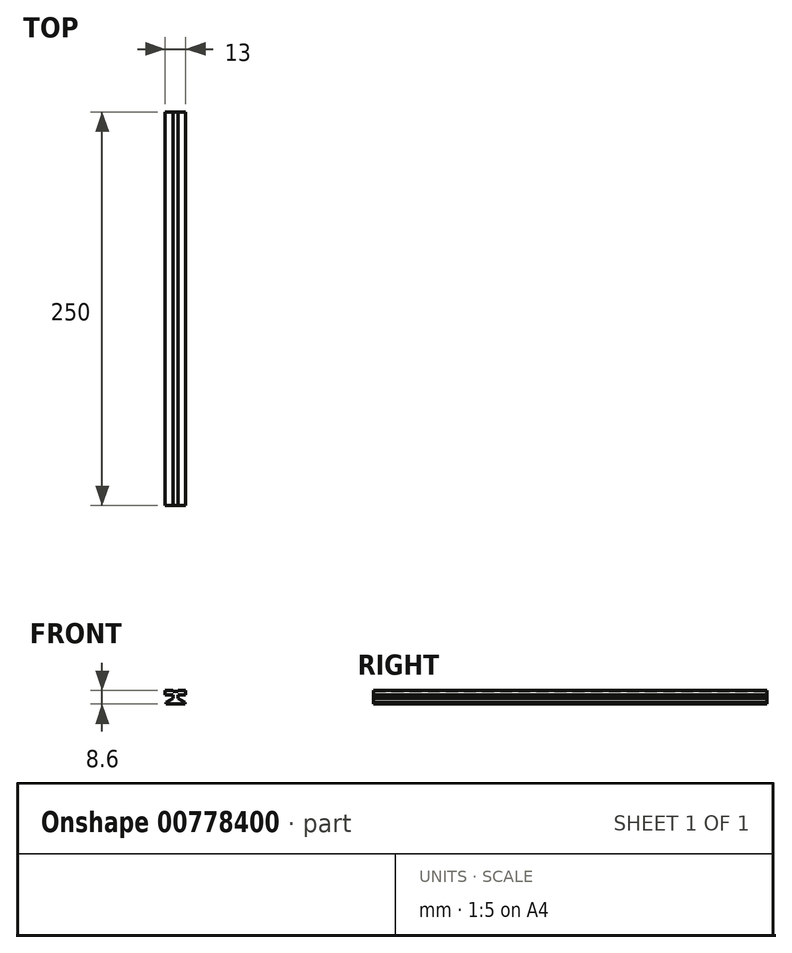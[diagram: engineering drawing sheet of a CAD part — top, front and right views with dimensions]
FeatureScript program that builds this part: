
annotation { "Feature Type Name" : "Feature", "Feature Type Description" : "" }
export const myFeature = defineFeature(function(context is Context, id is Id, definition is map)
    precondition{}
    {
        {
            var Q0;
            Q0=qCreatedBy(makeId("Front.planeOp"),FACE);
            var sketch = newSketch(context, id + "F0", { "sketchPlane" : qUnion([Q0])});
            skLineSegment(sketch, "E0.bottom", {"start": v(6, 0) * mm, "end": v(-6, 0) * mm});
            skLineSegment(sketch, "E0.top", {"start": v(6, 1) * mm, "end": v(-6, 1) * mm});
            skLineSegment(sketch, "E0.left", {"start": v(6, 0) * mm, "end": v(6, 1) * mm});
            skLineSegment(sketch, "E0.right", {"start": v(-6, 0) * mm, "end": v(-6, 1) * mm});
            skLineSegment(sketch, "E1", {"start": v(0, 0) * mm, "end": v(0, 5.9) * mm});
            skLineSegment(sketch, "E2", {"start": v(0, 5.9) * mm, "end": v(0, 8.6) * mm});
            skLineSegment(sketch, "E3", {"start": v(-6.5, 8.6) * mm, "end": v(6.5, 8.6) * mm});
            skLineSegment(sketch, "E4", {"start": v(-6.5, 5.9) * mm, "end": v(6.5, 5.9) * mm});
            skLineSegment(sketch, "E5", {"start": v(-6.5, 8.6) * mm, "end": v(-6.5, 5.9) * mm});
            skLineSegment(sketch, "E6", {"start": v(6.5, 8.6) * mm, "end": v(6.5, 5.9) * mm});
            skLineSegment(sketch, "E7.bottom", {"start": v(-1.5, 5.9) * mm, "end": v(1.5, 5.9) * mm});
            skLineSegment(sketch, "E7.top", {"start": v(-1.5, 1) * mm, "end": v(1.5, 1) * mm});
            skLineSegment(sketch, "E7.left", {"start": v(-1.5, 5.9) * mm, "end": v(-1.5, 1) * mm});
            skLineSegment(sketch, "E7.right", {"start": v(1.5, 5.9) * mm, "end": v(1.5, 1) * mm});
            skPoint(sketch, "E8", {"position": v(-1.5, 3.45) * mm});
            skPoint(sketch, "E9", {"position": v(1.5, 3.45) * mm});
            skLineSegment(sketch, "E10", {"start": v(-1.5, 3.45) * mm, "end": v(-6, 1) * mm});
            skLineSegment(sketch, "E11", {"start": v(1.5, 3.45) * mm, "end": v(6, 1) * mm});
            skLineSegment(sketch, "E12", {"start": v(-1.5, 8.6) * mm, "end": v(-1.5, 8.1) * mm});
            skLineSegment(sketch, "E13", {"start": v(-1.5, 8.1) * mm, "end": v(1.5, 8.1) * mm});
            skLineSegment(sketch, "E14", {"start": v(1.5, 8.1) * mm, "end": v(1.5, 8.6) * mm});
            skSolve(sketch);
        }
        {
            var Q0;
            {var subQ0=sQuery(id+"F0.wireOp",EDGE,"E11");Q0=makeQuery(id+"F0.imprint","IMPRINT",FACE,{"disambiguationData":[TD([[makeQuery(id+"F0.imprint","IMPRINT",EDGE,{"derivedFrom":subQ0}),-1.0]])]});}
            var Q1;
            {var subQ0=sQuery(id+"F0.wireOp",EDGE,"E10");Q1=makeQuery(id+"F0.imprint","IMPRINT",FACE,{"disambiguationData":[TD([[makeQuery(id+"F0.imprint","IMPRINT",EDGE,{"derivedFrom":subQ0}),1.0]])]});}
            var Q2;
            {var subQ5=sQuery(id+"F0.wireOp",EDGE,"E0.left");Q2=makeQuery(id+"F0.imprint","IMPRINT",FACE,{"disambiguationData":[TD([[makeQuery(id+"F0.imprint","IMPRINT",EDGE,{"derivedFrom":subQ5}),1.0]])]});}
            var Q3;
            {var subQ0=sQuery(id+"F0.wireOp",EDGE,"E0.right");Q3=makeQuery(id+"F0.imprint","IMPRINT",FACE,{"disambiguationData":[TD([[makeQuery(id+"F0.imprint","IMPRINT",EDGE,{"derivedFrom":subQ0}),-1.0]])]});}
            var Q4;
            {var subQ4=sQuery(id+"F0.wireOp",EDGE,"E1");var subQ6=sQuery(id+"F0.wireOp",EDGE,"E7.top");var subQ8=makeQuery(id+"F0.imprint","INTERSECT",VERTEX,{"derivedFrom":[subQ4,subQ6]});Q4=makeQuery(id+"F0.imprint","IMPRINT",FACE,{"disambiguationData":[TD([[makeQuery(id+"F0.imprint","IMPRINT",EDGE,{"disambiguationData":[TD([[subQ8,-1.0]])],"derivedFrom":subQ4}),1.0]])]});}
            var Q5;
            {var subQ1=sQuery(id+"F0.wireOp",EDGE,"E7.top");var subQ3=sQuery(id+"F0.wireOp",EDGE,"E1");var subQ4=makeQuery(id+"F0.imprint","INTERSECT",VERTEX,{"derivedFrom":[subQ3,subQ1]});Q5=makeQuery(id+"F0.imprint","IMPRINT",FACE,{"disambiguationData":[TD([[makeQuery(id+"F0.imprint","IMPRINT",EDGE,{"disambiguationData":[TD([[subQ4,-1.0]])],"derivedFrom":subQ3}),-1.0]])]});}
            var Q6;
            {var subQ0=sQuery(id+"F0.wireOp",EDGE,"E5");Q6=makeQuery(id+"F0.imprint","IMPRINT",FACE,{"disambiguationData":[TD([[makeQuery(id+"F0.imprint","IMPRINT",EDGE,{"derivedFrom":subQ0}),1.0]])]});}
            var Q7;
            {var subQ0=sQuery(id+"F0.wireOp",EDGE,"E6");Q7=makeQuery(id+"F0.imprint","IMPRINT",FACE,{"disambiguationData":[TD([[makeQuery(id+"F0.imprint","IMPRINT",EDGE,{"derivedFrom":subQ0}),-1.0]])]});}
            extrude(context, id + "F1", {"entities" : qUnion([Q0, Q1, Q2, Q3, Q4, Q5, Q6, Q7]), "depth" : 250 * mm, "offsetDistance" : 25 * mm});
        }
    });
